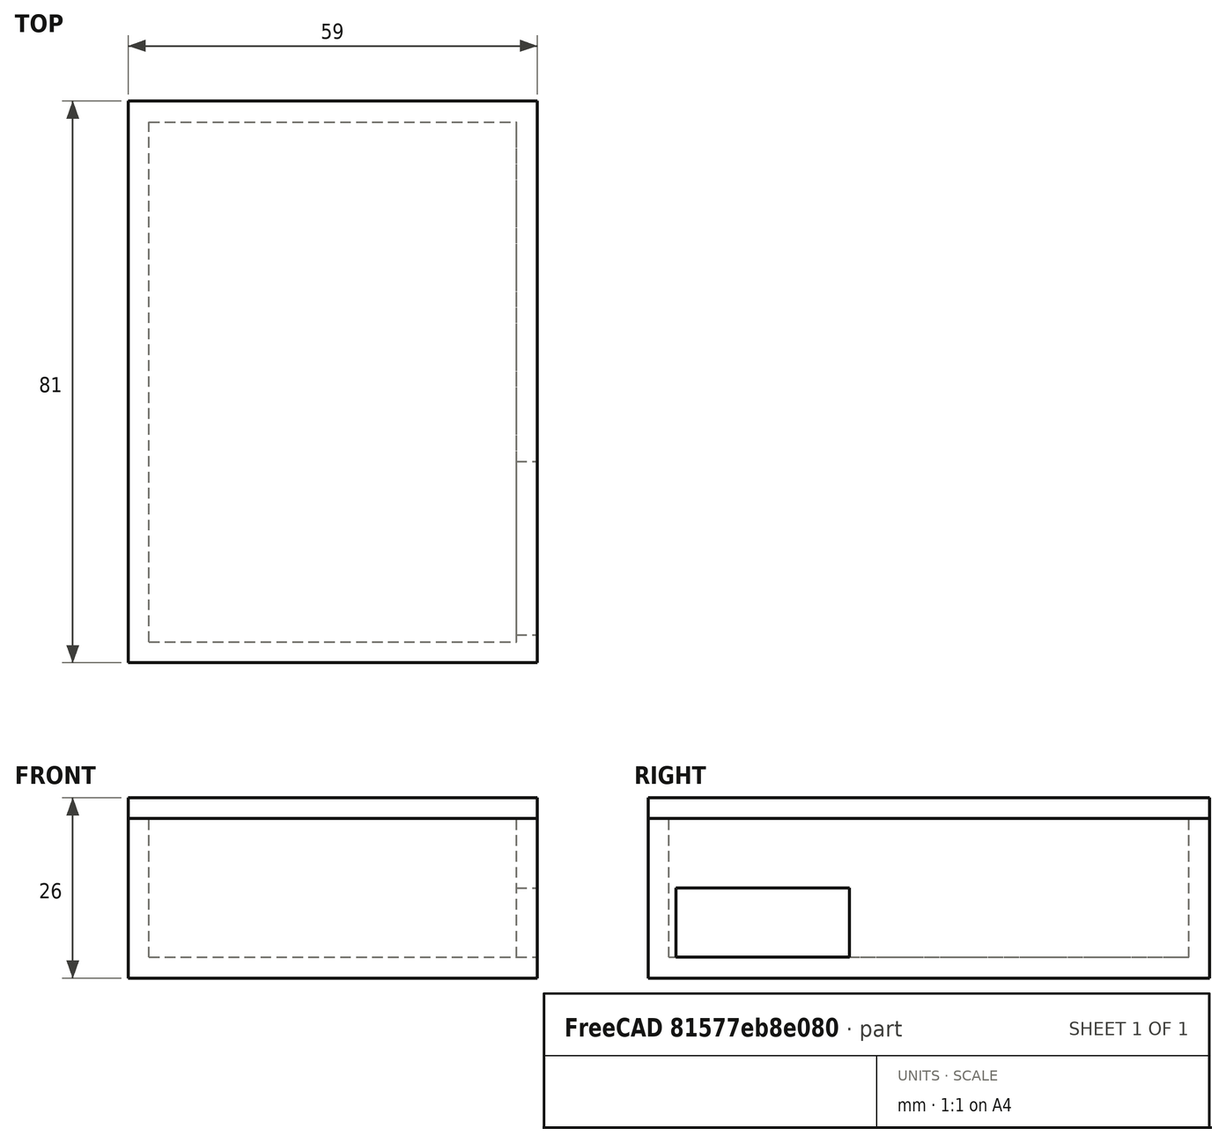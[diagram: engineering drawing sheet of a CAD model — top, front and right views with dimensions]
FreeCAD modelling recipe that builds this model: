
FCSTD DOCUMENT  (FreeCAD 0.16R6706 (Git))
Label: pcb
License: All rights reserved
LicenseURL: http://en.wikipedia.org/wiki/All_rights_reserved
objects: Part::Box×5, Part::Cut×2, Part::MultiFuse×1
note: 8 computed .brp shape members not serialized (recipe doc carries the construction recipe); baked Part::Feature solids carry a one-line shape summary decoded from their .brp

FEATURE [Part::Box] Box  label="1"
  Height = 20
  Length = 59
  Width = 81
FEATURE [Part::Box] Box001  label="2"
  Height = 20
  Length = 53
  Placement = pos=(3,3,0) rot=(0,0,1;0rad)
  Width = 75
FEATURE [Part::Cut] Cut
  Base = -> Box
  Placement = pos=(0,0,3) rot=(0,0,1;0rad)
  Tool = -> Box001
FEATURE [Part::Box] Box002  label="3"
  Height = 3
  Length = 59
  Width = 81
FEATURE [Part::Box] Box003  label="4"
  Height = 10
  Length = 3
  Placement = pos=(56,4,3) rot=(0,0,1;0rad)
  Width = 25
FEATURE [Part::MultiFuse] Fusion  label="5"
  Shapes = -> [Cut,Box002]
FEATURE [Part::Cut] Cut001  label="caja"
  Base = -> Fusion
  Tool = -> Box003
FEATURE [Part::Box] Box004  label="tapa"
  Height = 3
  Length = 59
  Placement = pos=(0,0,23) rot=(0,0,1;0rad)
  Width = 81
